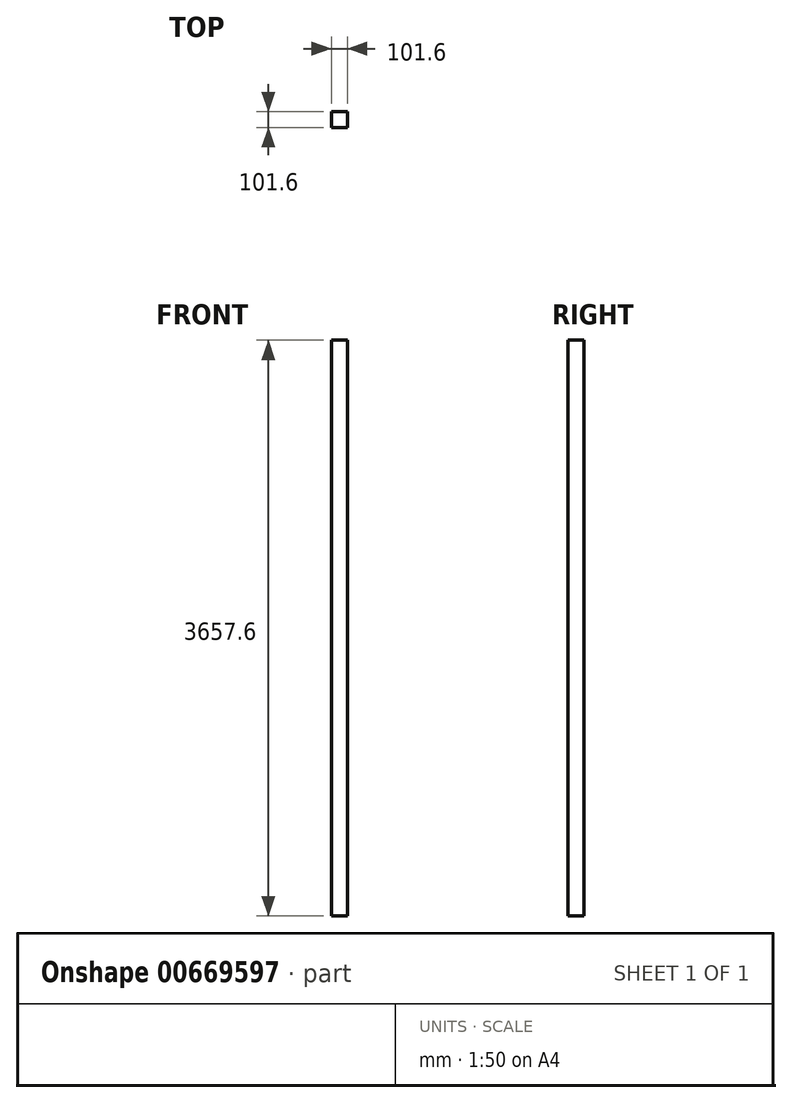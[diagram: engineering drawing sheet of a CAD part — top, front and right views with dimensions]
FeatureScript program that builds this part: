
annotation { "Feature Type Name" : "Feature", "Feature Type Description" : "" }
export const myFeature = defineFeature(function(context is Context, id is Id, definition is map)
    precondition{}
    {
        {
            var Q0;
            Q0=qCreatedBy(makeId("Top.planeOp"),FACE);
            var sketch = newSketch(context, id + "F0", { "sketchPlane" : qUnion([Q0])});
            skLineSegment(sketch, "E0.bottom", {"start": v(-50.8, 50.8) * mm, "end": v(50.8, 50.8) * mm});
            skLineSegment(sketch, "E0.top", {"start": v(-50.8, -50.8) * mm, "end": v(50.8, -50.8) * mm});
            skLineSegment(sketch, "E0.left", {"start": v(-50.8, 50.8) * mm, "end": v(-50.8, -50.8) * mm});
            skLineSegment(sketch, "E0.right", {"start": v(50.8, 50.8) * mm, "end": v(50.8, -50.8) * mm});
            skSolve(sketch);
        }
        {
            var Q0;
            Q0 = qSketchRegion(id + "F0", true);
            extrude(context, id + "F1", {"entities" : qUnion([Q0]), "depth" : 3657.6 * mm, "offsetDistance" : 25.4 * mm});
        }
    });
